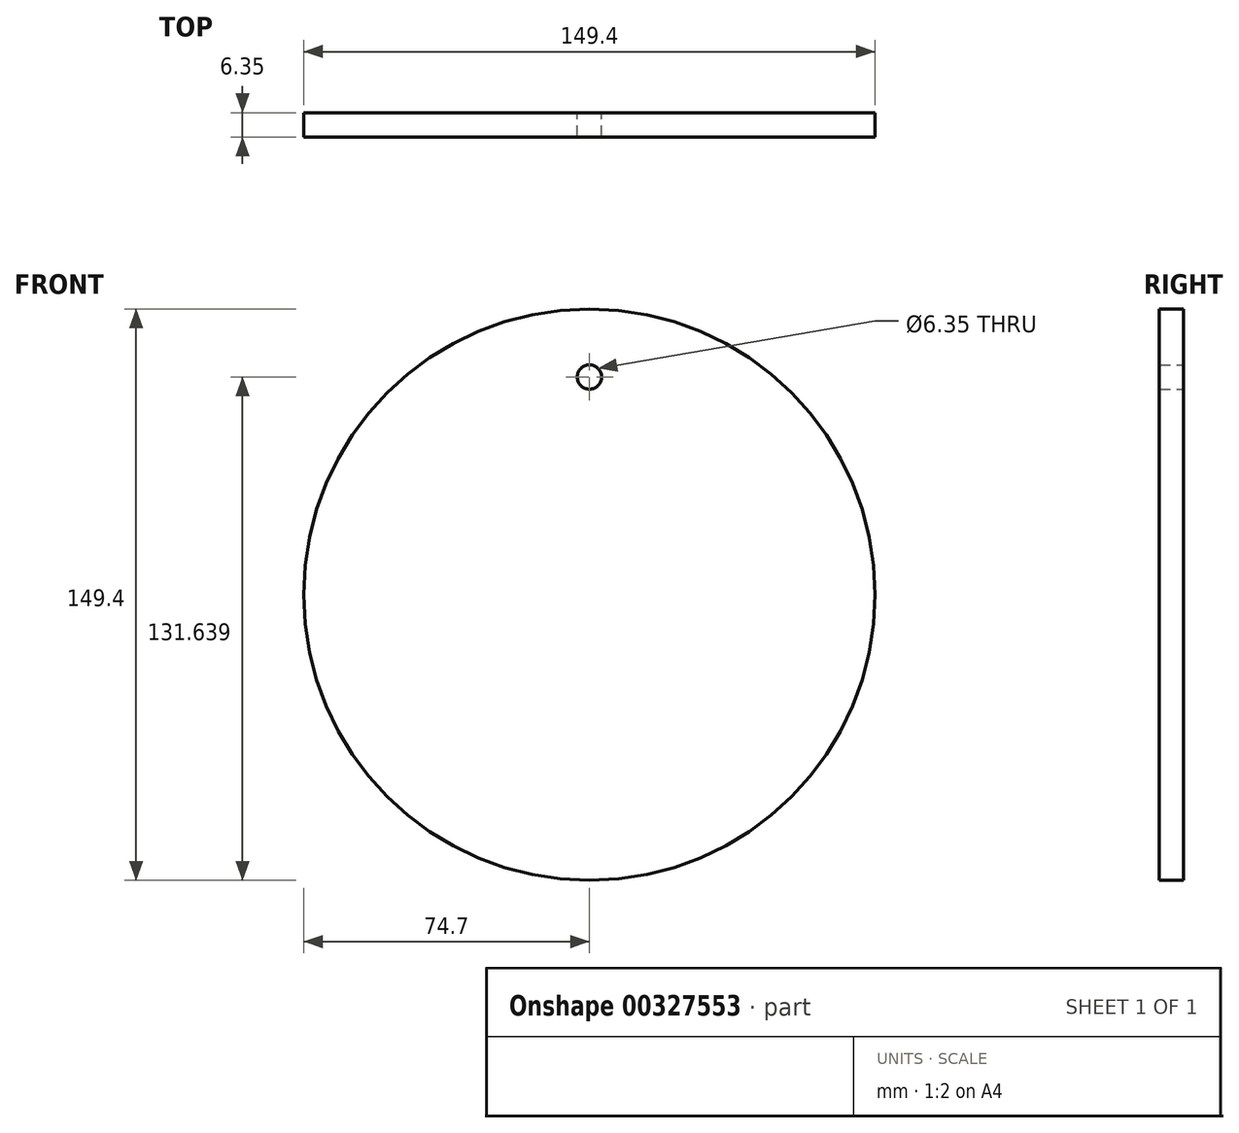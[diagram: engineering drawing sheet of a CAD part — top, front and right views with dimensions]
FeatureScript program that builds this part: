
annotation { "Feature Type Name" : "Feature", "Feature Type Description" : "" }
export const myFeature = defineFeature(function(context is Context, id is Id, definition is map)
    precondition{}
    {
        {
            var Q0;
            Q0=qCreatedBy(makeId("Front.planeOp"),FACE);
            var sketch = newSketch(context, id + "F0", { "sketchPlane" : qUnion([Q0])});
            skCircle(sketch, "E0", {"center": v(0, 0) * mm, "radius": 74.7 * mm});
            skSolve(sketch);
        }
        {
            var Q0;
            Q0=makeQuery(id+"F0.imprint","IMPRINT",FACE,{"disambiguationData":[TD([[makeQuery(id+"F0.imprint","IMPRINT",EDGE,{"derivedFrom":sQuery(id+"F0.wireOp",EDGE,"E0")}),1.0]])]});
            var sketch = newSketch(context, id + "F1", { "sketchPlane" : qUnion([Q0])});
            skCircle(sketch, "E1", {"center": v(0, 56.94) * mm, "radius": 10.68 * mm});
            skCircle(sketch, "E2.1.0", {"center": v(-28.47, 49.31) * mm, "radius": 10.68 * mm});
            skCircle(sketch, "E2.2.0", {"center": v(-49.31, 28.47) * mm, "radius": 10.68 * mm});
            skCircle(sketch, "E2.3.0", {"center": v(-56.94, 0) * mm, "radius": 10.68 * mm});
            skCircle(sketch, "E2.4.0", {"center": v(-49.31, -28.47) * mm, "radius": 10.68 * mm});
            skCircle(sketch, "E2.5.0", {"center": v(-28.47, -49.31) * mm, "radius": 10.68 * mm});
            skCircle(sketch, "E2.6.0", {"center": v(0, -56.94) * mm, "radius": 10.68 * mm});
            skCircle(sketch, "E2.7.0", {"center": v(28.47, -49.31) * mm, "radius": 10.68 * mm});
            skCircle(sketch, "E2.8.0", {"center": v(49.31, -28.47) * mm, "radius": 10.68 * mm});
            skCircle(sketch, "E2.9.0", {"center": v(56.94, 0) * mm, "radius": 10.68 * mm});
            skCircle(sketch, "E2.10.0", {"center": v(49.31, 28.47) * mm, "radius": 10.68 * mm});
            skCircle(sketch, "E2.11.0", {"center": v(28.47, 49.31) * mm, "radius": 10.68 * mm});
            skPoint(sketch, "E2.center", {"position": v(0, 0) * mm});
            skSolve(sketch);
        }
        {
            var Q0;
            Q0=makeQuery(id+"F0.imprint","IMPRINT",FACE,{"disambiguationData":[TD([[makeQuery(id+"F0.imprint","IMPRINT",EDGE,{"derivedFrom":sQuery(id+"F0.wireOp",EDGE,"E0")}),1.0]])]});
            extrude(context, id + "F2", {"entities" : qUnion([Q0]), "depth" : 6.35 * mm});
        }
        {
            var Q0;
            Q0=sQuery(id+"F1.wireOp",VERTEX,"E1.center");
            var Q1;
            Q1=makeQuery(id+"F2.opExtrude","SWEPT_BODY",BODY,{"disambiguationData":[OSD([sQuery(id+"F0.wireOp",EDGE,"E0")])]});
            hole(context, id + "F3", {"style" : HoleStyle.SIMPLE, "endStyle" : HoleEndStyle.THROUGH, "oppositeDirection" : true, "holeDiameter" : 6.35 * mm, "tappedDepth" : 12.7 * mm, "tapClearance" : 3, "locations" : qUnion([Q0]), "scope" : qUnion([Q1])});
        }
    });
